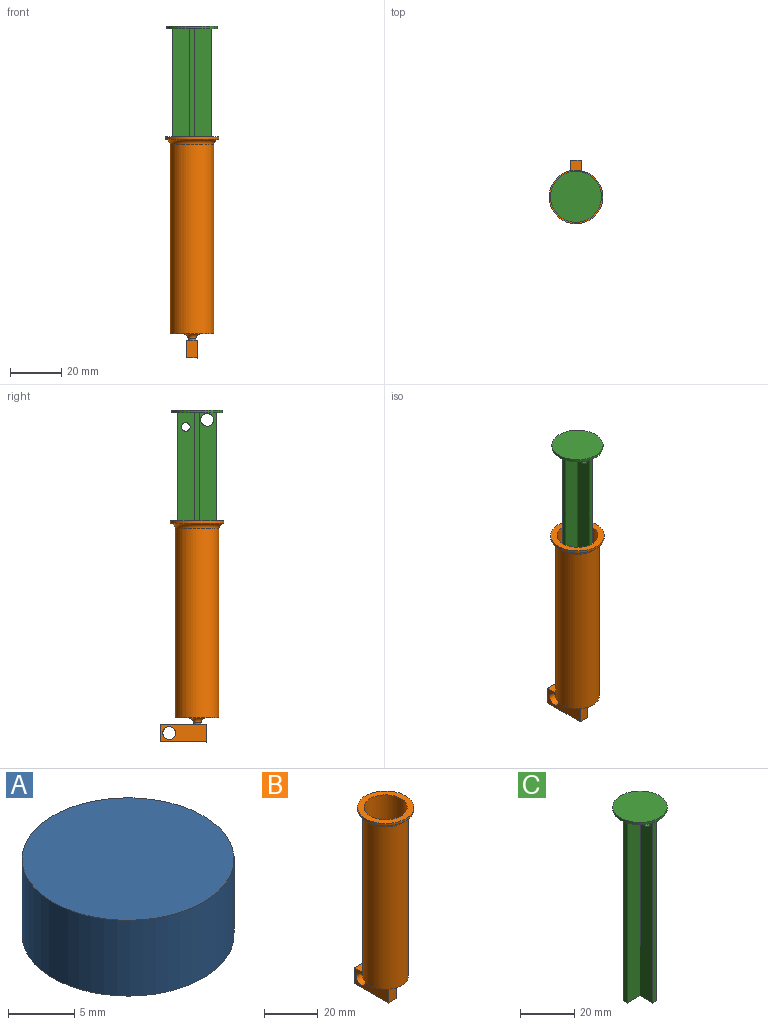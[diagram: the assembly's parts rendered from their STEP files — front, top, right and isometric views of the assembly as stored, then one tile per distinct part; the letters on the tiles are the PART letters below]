
ASSEMBLY  parts=3 mates=2
PART A: 3 faces, bbox 16x16x7 mm
  f0: cylinder r=8mm len=16mm, axis (0,0,1), area 351.9mm2, adj f1,f2
  f1: plane 16x16mm, normal (0,0,-1), area 201.1mm2, adj f0
  f2: plane 16x16mm, normal (0,0,1), area 201.1mm2, adj f0
PART B: 19 faces, bbox 22.7x25.9x86.5 mm
  f0: cylinder r=1.5mm len=3mm, axis (0,0,1), area 4.7mm2, adj f7,f17
  f1: cylinder r=8mm len=76mm, axis (0,0,-1), area 3820.2mm2, adj f3,f9
  f2: cylinder r=8.5mm len=74mm, axis (0,0,-1), area 3952.1mm2, adj f6,f10
  f3: plane 16x16mm, normal (0,0,1), area 197.9mm2, adj f1,f4
  f4: cylinder r=1mm len=7mm, axis (0,0,1), area 44mm2, adj f3,f5
  f5: plane 3x3mm, normal (0,0,-1), area 3.9mm2, adj f4,f11
  f6: plane 17x17mm, normal (0,0,-1), area 188.5mm2, adj f2,f7
  f7: torus R=3.5mm, axis (0,0,1), area 44mm2, adj f0,f6
  f8: cylinder r=10.5mm len=21mm, axis (0,0,-1), area 66mm2, adj f9,f10
  f9: plane 21x21mm, normal (0,0,1), area 145.3mm2, adj f1,f8
  f10: torus R=10.5mm, axis (0,0,1), area 182.1mm2, adj f2,f8
  f11: cylinder r=1.5mm len=3.5mm, axis (0,0,1), area 33mm2, adj f5,f16
  f12: plane 18x7mm, normal (-1,0,0), area 106.4mm2, adj f13,f15,f16,f17,f18
  f13: plane 7x4mm, normal (0,1,0), area 28mm2, adj f12,f14,f16,f17
  f14: plane 18x7mm, normal (1,0,0), area 106.4mm2, adj f13,f15,f16,f17,f18
  f15: plane 7x4mm, normal (0,-1,0), area 28mm2, adj f12,f14,f16,f17
  f16: plane 18x4mm, normal (0,0,-1), area 64.9mm2, adj f11,f12,f13,f14,f15
  f17: plane 18x4mm, normal (0,0,1), area 64.9mm2, adj f0,f12,f13,f14,f15
  f18: cylinder r=2.5mm len=5mm, axis (-1,0,0), area 62.8mm2, adj f12,f14
PART C: 18 faces, bbox 20x20x84 mm
  f0: plane 83x6.5mm, normal (0,1,0), area 539.5mm2, adj f1,f11,f12,f15
  f1: plane 83x2mm, normal (-1,0,0), area 166mm2, adj f0,f2,f12,f15
  f2: plane 83x6.5mm, normal (0,-1,0), area 539.5mm2, adj f1,f3,f12,f15
  f3: plane 83x6.5mm, normal (-1,0,0), area 519.9mm2, adj f2,f4,f12,f15,f17
  f4: plane 83x2mm, normal (0,-1,0), area 166mm2, adj f3,f5,f12,f15
  f5: plane 83x6.5mm, normal (1,0,0), area 519.9mm2, adj f4,f6,f12,f15,f17
  f6: plane 83x6.5mm, normal (0,-1,0), area 539.5mm2, adj f5,f7,f12,f15
  f7: plane 83x2mm, normal (1,0,0), area 166mm2, adj f6,f8,f12,f15
  f8: plane 83x6.5mm, normal (0,1,0), area 539.5mm2, adj f7,f9,f12,f15
  f9: plane 83x6.5mm, normal (1,0,0), area 530.4mm2, adj f8,f10,f12,f15,f16
  f10: plane 83x2mm, normal (0,1,0), area 166mm2, adj f9,f11,f12,f15
  f11: plane 83x6.5mm, normal (-1,0,0), area 530.4mm2, adj f0,f10,f12,f15,f16
  f12: plane 15x15mm, normal (0,0,-1), area 56mm2, adj f0,f1,f2,f3,f4,f5,f6,f7
  f13: cylinder r=10mm len=20mm, axis (0,0,-1), area 62.8mm2, adj f14,f15
  f14: plane 20x20mm, normal (0,0,1), area 314.2mm2, adj f13
  f15: plane 20x20mm, normal (0,0,-1), area 258.2mm2, adj f0,f1,f2,f3,f4,f5,f6,f7
  f16: cylinder r=1.7mm len=3.4mm, axis (-1,0,0), area 21.4mm2, adj f9,f11
  f17: cylinder r=2.5mm len=5mm, axis (-1,0,0), area 31.4mm2, adj f3,f5
PLACE A t=(-50.72,-57.91,-15.83)mm
PLACE B rot(axis=(0.69,0.45,0.56),0deg) t=(-50.72,-57.91,-51.21)mm fixed
PLACE C rot(axis=(0.69,0.45,0.56),0deg) t=(-50.72,-57.91,-15.83)mm
MATE fastened C.f13 <-> A.f0  axis (0,0,-1) through (-50.72,-57.91,-15.83)mm
MATE slider B.f1 <-> A.f0  axis (0,0,-1) through (-50.72,-57.91,24.79)mm
